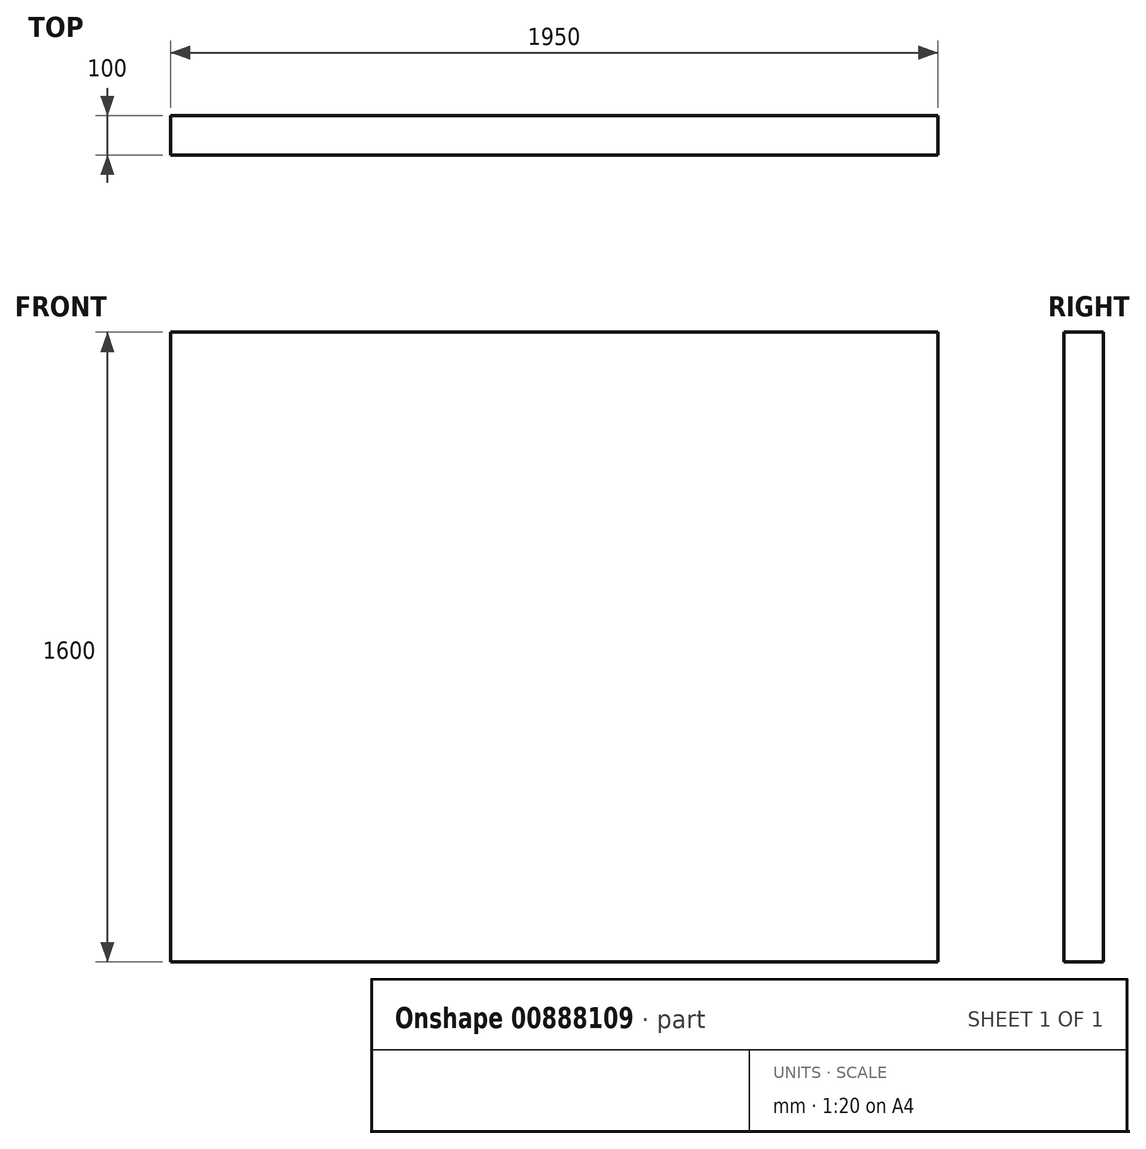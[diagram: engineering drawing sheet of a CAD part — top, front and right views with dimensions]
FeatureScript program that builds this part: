
annotation { "Feature Type Name" : "Feature", "Feature Type Description" : "" }
export const myFeature = defineFeature(function(context is Context, id is Id, definition is map)
    precondition{}
    {
        {
            var Q0;
            Q0=qCreatedBy(makeId("Front.planeOp"),FACE);
            var sketch = newSketch(context, id + "F0", { "sketchPlane" : qUnion([Q0])});
            skLineSegment(sketch, "E0.bottom", {"start": v(-952.4, 1175.99) * mm, "end": v(997.6, 1175.99) * mm});
            skLineSegment(sketch, "E0.top", {"start": v(-952.4, -424.01) * mm, "end": v(997.6, -424.01) * mm});
            skLineSegment(sketch, "E0.left", {"start": v(-952.4, 1175.99) * mm, "end": v(-952.4, -424.01) * mm});
            skLineSegment(sketch, "E0.right", {"start": v(997.6, 1175.99) * mm, "end": v(997.6, -424.01) * mm});
            skSolve(sketch);
        }
        {
            var Q0;
            Q0=makeQuery(id+"F0.imprint","IMPRINT",FACE,{"disambiguationData":[TD([[makeQuery(id+"F0.imprint","IMPRINT",EDGE,{"derivedFrom":sQuery(id+"F0.wireOp",EDGE,"E0.bottom")}),-1.0]])]});
            extrude(context, id + "F1", {"entities" : qUnion([Q0]), "depth" : 100 * mm, "offsetDistance" : 25 * mm});
        }
    });
